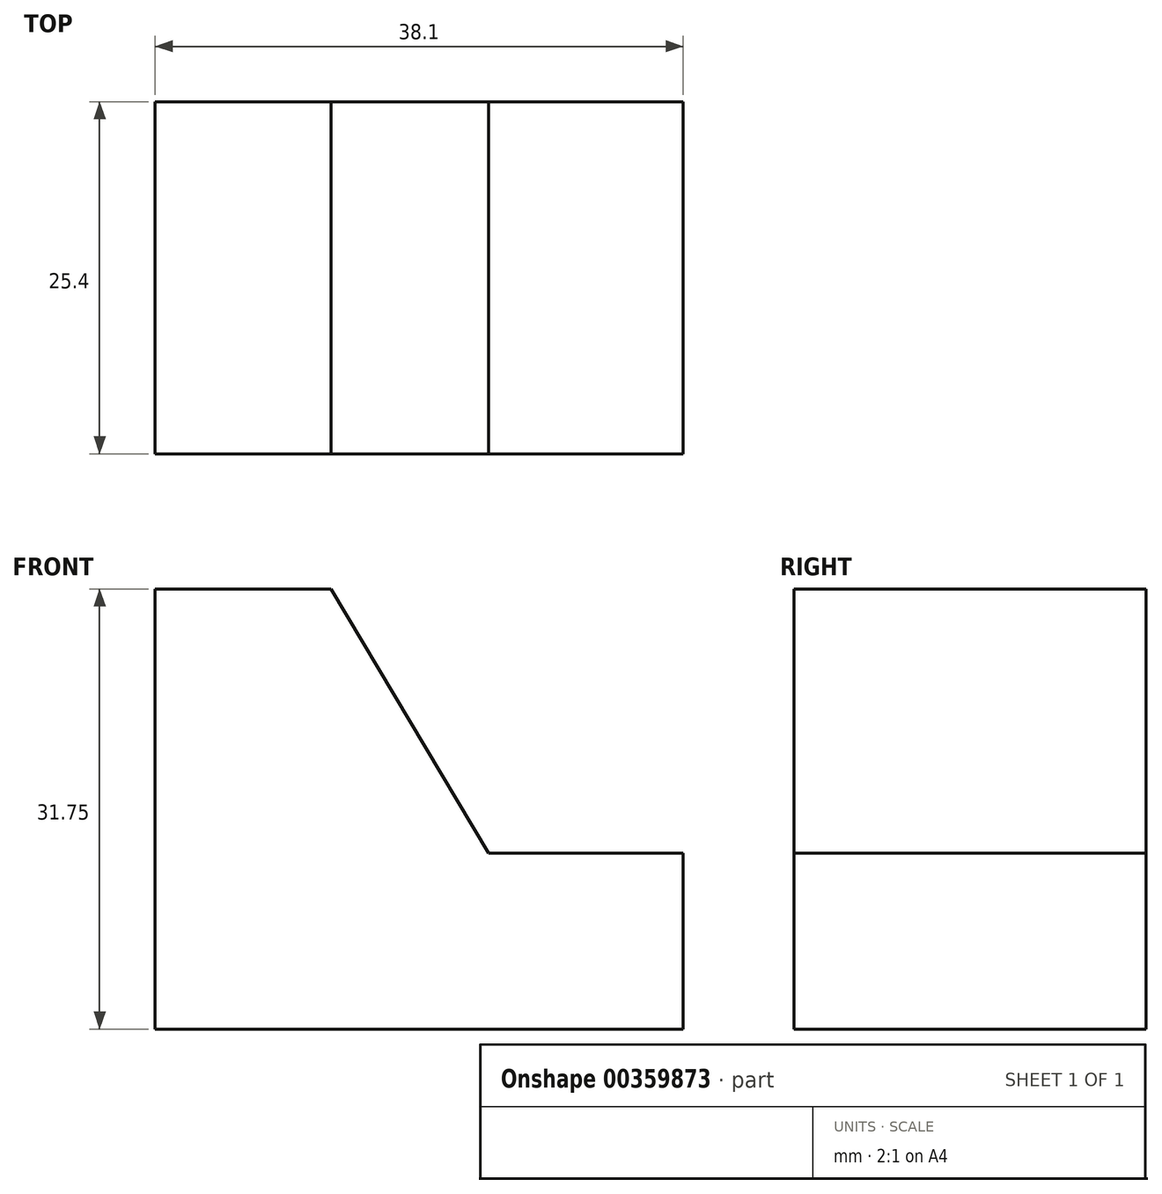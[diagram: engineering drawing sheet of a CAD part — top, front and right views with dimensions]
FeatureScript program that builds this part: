
annotation { "Feature Type Name" : "Feature", "Feature Type Description" : "" }
export const myFeature = defineFeature(function(context is Context, id is Id, definition is map)
    precondition{}
    {
        {
            var Q0;
            Q0=qCreatedBy(makeId("Front.planeOp"),FACE);
            var sketch = newSketch(context, id + "F0", { "sketchPlane" : qUnion([Q0])});
            skLineSegment(sketch, "E0", {"start": v(-5.62, 0) * mm, "end": v(-5.62, 31.75) * mm});
            skLineSegment(sketch, "E1", {"start": v(-5.62, 31.75) * mm, "end": v(32.48, 31.75) * mm});
            skLineSegment(sketch, "E2", {"start": v(32.48, 31.75) * mm, "end": v(32.48, 0) * mm});
            skLineSegment(sketch, "E3", {"start": v(-5.62, 0) * mm, "end": v(32.48, 0) * mm});
            skSolve(sketch);
        }
        {
            var Q0;
            Q0 = qSketchRegion(id + "F0", true);
            extrude(context, id + "F1", {"entities" : qUnion([Q0]), "depth" : 25.4 * mm});
        }
        {
            var Q0;
            Q0=makeQuery(id+"F1.opExtrude","CAP_FACE",FACE,{"disambiguationData":[OSD([sQuery(id+"F0.wireOp",EDGE,"E0"),sQuery(id+"F0.wireOp",EDGE,"E1"),sQuery(id+"F0.wireOp",EDGE,"E2"),sQuery(id+"F0.wireOp",EDGE,"E3")])],"isStart":false});
            var sketch = newSketch(context, id + "F2", { "sketchPlane" : qUnion([Q0])});
            skLineSegment(sketch, "E4", {"start": v(7.08, 31.75) * mm, "end": v(18.43, 12.7) * mm});
            skLineSegment(sketch, "E5", {"start": v(18.43, 12.7) * mm, "end": v(32.48, 12.7) * mm});
            skSolve(sketch);
        }
        {
            var Q0;
            {var subQ0=sQuery(id+"F2.wireOp",EDGE,"E4");Q0=makeQuery(id+"F2.imprint","IMPRINT",FACE,{"disambiguationData":[TD([[makeQuery(id+"F2.imprint","IMPRINT",EDGE,{"derivedFrom":subQ0}),1.0]])]});}
            extrude(context, id + "F3", {"entities" : qUnion([Q0]), "operationType" : NewBodyOperationType.REMOVE, "oppositeDirection" : true, "depth" : 25.4 * mm});
        }
    });
